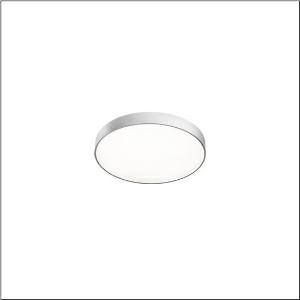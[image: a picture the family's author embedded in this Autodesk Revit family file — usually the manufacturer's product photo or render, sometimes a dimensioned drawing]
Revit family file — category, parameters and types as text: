
# Revit family: round_21_s_51mr34fd0321s
name_source: partatom
category: Lighting Fixtures
units: mm (PartAtom-declared; Revit-internal decimal feet)

## family parameters
Cut with Voids When Loaded = No
Host = Face
Light Source = No
Part Type = Normal
Room Calculation Point = No
Round Connector Dimension = Use Diameter
Shared = No

## types (1)
- Round 21 S (1 x LED, 3750 lm, 30.3 W, 3000K)
    Apparent Load = 30 VA
    CIE Flux Codes = 49 80 96 100 100
    Color Rendering = 80
    Color Temperature = 3000K
    Default Elevation = 1800 mm
    Description = Round 21 S, wall and ceiling luminaire, primary optical cover: cover, of PMMA, opal, light emission: direct distribution, primary light characteristic: symmetric, installation type: suspended mounting, surface-mounted, LED, rated luminous flux: 3.750lm, luminous efficacy: 124lm/W, light colour: 830, colour temperature: 3000K, control gear: DALI 2, with terminal, 5-pole, mains connection: 230V, AC, 50/60Hz, rated input power: 30.3W, housing, of aluminium, coated, silver, diameter: 400mm, height: 62mm, protection rating (complete): IP40, insulation class (complete): insulation class I (protective earthing), certification: CE, impact resistance: IK04, permissible operating ambient temperature: -10..+35°C, packaging unit: 1 piece
    Height = 87 mm
    Lamp = 1 x LED
    Lamp Light Flux = 3750 lm
    Lamp Power = 30.3 W
    Lamp count = 1
    Length = 400 mm
    Luminous efficacy = 124 lm/W
    Manufacturer = Siteco
    ModVariant = No
    Model = 51MR34FD0321S
    Mounting Place = Wall
    Mounting Type = Surface mounted
    Number of Poles = 1
    OnlyDefault = Yes
    Power Factor = 1
    Product Name = Round 21 S
    Product group = wall and ceiling luminaire
    ProductGroupID = 2001
    Protection Class = Protection class I
    Protection Degree = IP 40
    RLX_Detail_Level = 1
    RLX_Emergency_Light_Flux = 0 lm
    RLX_Emergency_Type = 0
    RLX_Emergency_Type_DB = No
    RlxData = <blob elided: 11169 chars, md5=f8d29423>
    Socket = socket
    Standby Power = 0 W
    System Light Flux = 3750 lm
    System Power = 30 W
    Type Comments = Product without accessories
    Type Image = l_1258309.jpg
    URL = http://relux.com
    VarID = ---
    Voltage = 0 V
    Weight = 0.00 kg
    Width = 0 mm  [stored 0 ft]

note: [stored X ft] marks values corroborated as IEEE doubles in the binary element streams (Revit-internal decimal feet)

## geometry (parser evidence)
native form markers: Sweep x8
no freeform markers — native parametric forms only
